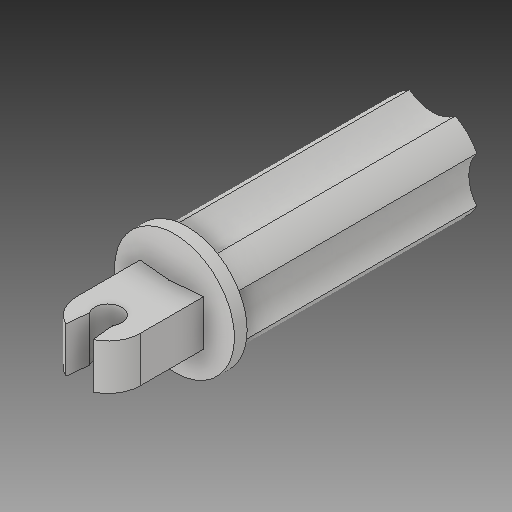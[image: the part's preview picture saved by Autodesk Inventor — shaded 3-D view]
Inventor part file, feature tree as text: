
AUTODESK INVENTOR PART (.ipt)
format: ipt  version: 2019 (Build 230136000, 136)  size: 184,320 bytes
history: native  units: in
note: dims shown in document units (in); Inventor stores cm internally (conversion verified against a paired STEP export)
features: sketch x6, extrude x5, pattern_circular x1, revolve x1
ambient origin geometry x8: Origin, YZ Plane, XZ Plane, XY Plane, X Axis, Y Axis, Z Axis, Center Point
bodies: Solid1 (feature_tree)
feature tree (13):
  extrude  "Extrusion1"  Depth=1.35in TaperAngle=0.0deg
  extrude  "Extrusion2"  Depth=1.43in TaperAngle=0.0deg
  extrude  "Extrusion3"  Depth=0.2in
  pattern_circular  "Circular Pattern1"  Count=4 Angle=360.0deg
  revolve  "Revolution1"  [1 undecoded]
  extrude  "Extrusion4"  TaperAngle=90.0deg  [1 undecoded]
  extrude  "Extrusion5"  Depth=0.35in
  sketch  "Sketch1"  dims[d0=0.55in d1=1.35in d2=0.0in]
  sketch  "Sketch2"  dims[d3=0.134in d4=1.43in d5=0.0in]
  sketch  "Sketch3"  dims[d6=0.4in d7=0.2in]
  sketch  "Sketch4"  dims[d8=1.4925in d9=0.0in d10=1.5748in d11=360.0deg]
  sketch  "Sketch5"  dims[d13=0.33in d14=0.07in]
  sketch  "Sketch6"  dims[d15=0.1in d16=90.0deg d17=0.35in d18=0.35in d19=0.25in d20=0.0in d22=0.15in d23=0.125in d24=0.15in d25=0.25in d26=0.0in]
note: 2 required parameter values undecoded (feature->parameter linkage not recoverable at this tier; creation-order binding heuristic only, values carry confidence <= 0.55)